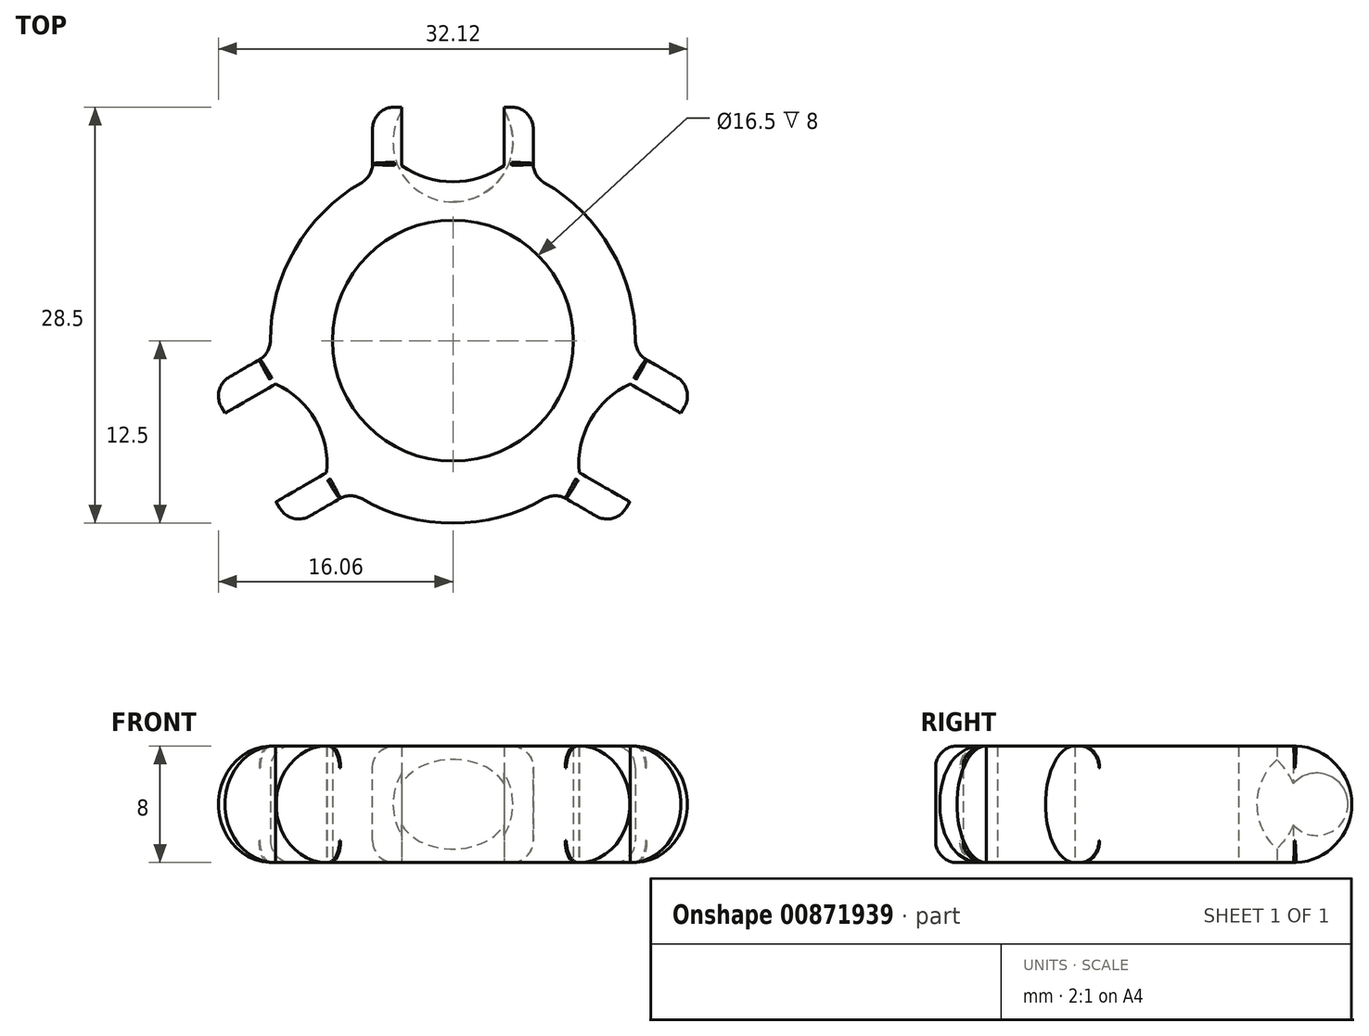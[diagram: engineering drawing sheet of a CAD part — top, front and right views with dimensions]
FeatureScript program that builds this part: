
annotation { "Feature Type Name" : "Feature", "Feature Type Description" : "" }
export const myFeature = defineFeature(function(context is Context, id is Id, definition is map)
    precondition{}
    {
        {
            var Q0;
            Q0=qCreatedBy(makeId("Top.planeOp"),FACE);
            var sketch = newSketch(context, id + "F0", { "sketchPlane" : qUnion([Q0])});
            skArc(sketch, "E0", {"start": v(-5.5, 11.22) * mm, "mid": v(-10.83, 6.25) * mm, "end": v(-12.47, -0.85) * mm});
            skLineSegment(sketch, "E1", {"start": v(0, 23.66) * mm, "end": v(0, -22.84) * mm, "construction": true});
            skLineSegment(sketch, "E2", {"start": v(-22.74, 0) * mm, "end": v(26.82, 0) * mm, "construction": true});
            skLineSegment(sketch, "E3", {"start": v(-3.5, 12) * mm, "end": v(-3.5, 16) * mm});
            skLineSegment(sketch, "E4", {"start": v(-3.5, 16) * mm, "end": v(-5.5, 16) * mm});
            skLineSegment(sketch, "E5", {"start": v(-5.5, 16) * mm, "end": v(-5.5, 11.22) * mm});
            skLineSegment(sketch, "E6.MirrorCS", {"start": v(3.5, 12) * mm, "end": v(3.5, 16) * mm});
            skLineSegment(sketch, "E7.MirrorCS", {"start": v(3.5, 16) * mm, "end": v(5.5, 16) * mm});
            skLineSegment(sketch, "E8.MirrorCS", {"start": v(5.5, 16) * mm, "end": v(5.5, 11.22) * mm});
            skLineSegment(sketch, "E9", {"start": v(-3.5, 12) * mm, "end": v(3.5, 12) * mm, "construction": true});
            skLineSegment(sketch, "E10", {"start": v(-3.5, 16) * mm, "end": v(3.5, 16) * mm, "construction": true});
            skPoint(sketch, "E11", {"position": v(0, 9.18) * mm});
            skLineSegment(sketch, "E12.1.0", {"start": v(-11.1, -12.76) * mm, "end": v(-6.97, -10.38) * mm});
            skLineSegment(sketch, "E12.1.1", {"start": v(-12.1, -11.03) * mm, "end": v(-11.1, -12.76) * mm});
            skLineSegment(sketch, "E12.1.2", {"start": v(-12.14, -2.97) * mm, "end": v(-15.6, -4.97) * mm});
            skLineSegment(sketch, "E12.1.3", {"start": v(-15.6, -4.97) * mm, "end": v(-16.6, -3.24) * mm});
            skLineSegment(sketch, "E12.1.4", {"start": v(-16.6, -3.24) * mm, "end": v(-12.47, -0.85) * mm});
            skLineSegment(sketch, "E12.1.5", {"start": v(-8.64, -9.03) * mm, "end": v(-12.1, -11.03) * mm});
            skLineSegment(sketch, "E12.2.0", {"start": v(16.6, -3.24) * mm, "end": v(12.47, -0.85) * mm});
            skLineSegment(sketch, "E12.2.1", {"start": v(15.6, -4.97) * mm, "end": v(16.6, -3.24) * mm});
            skLineSegment(sketch, "E12.2.2", {"start": v(8.64, -9.03) * mm, "end": v(12.1, -11.03) * mm});
            skLineSegment(sketch, "E12.2.3", {"start": v(12.1, -11.03) * mm, "end": v(11.1, -12.76) * mm});
            skLineSegment(sketch, "E12.2.4", {"start": v(11.1, -12.76) * mm, "end": v(6.97, -10.38) * mm});
            skLineSegment(sketch, "E12.2.5", {"start": v(12.14, -2.97) * mm, "end": v(15.6, -4.97) * mm});
            skArc(sketch, "E13.trimOffspring", {"start": v(12.47, -0.85) * mm, "mid": v(10.83, 6.25) * mm, "end": v(5.5, 11.22) * mm});
            skArc(sketch, "E14.trimOffspring", {"start": v(-6.97, -10.38) * mm, "mid": v(0, -12.5) * mm, "end": v(6.97, -10.38) * mm});
            skCircle(sketch, "E15", {"center": v(0, 0) * mm, "radius": 8.25 * mm});
            skArc(sketch, "E16", {"start": v(-3.5, 12) * mm, "mid": v(0, 10.87) * mm, "end": v(3.5, 12) * mm});
            skArc(sketch, "E17.1.0", {"start": v(-8.64, -9.03) * mm, "mid": v(-9.42, -5.44) * mm, "end": v(-12.14, -2.97) * mm});
            skArc(sketch, "E17.2.0", {"start": v(12.14, -2.97) * mm, "mid": v(9.42, -5.44) * mm, "end": v(8.64, -9.03) * mm});
            skSolve(sketch);
        }
        {
            var Q0;
            Q0=qCreatedBy(makeId("Front.planeOp"),FACE);
            var sketch = newSketch(context, id + "F1", { "sketchPlane" : qUnion([Q0])});
            skLineSegment(sketch, "E18", {"start": v(0, -15.32) * mm, "end": v(0, 34.97) * mm, "construction": true});
            skSolve(sketch);
        }
        {
            var Q0;
            Q0=qSketchRegion(id+"F0",true);
            extrude(context, id + "F2", {"entities" : qUnion([Q0]), "depth" : 8 * mm, "offsetDistance" : 25 * mm});
        }
        {
            var Q0;
            Q0=qCreatedBy(makeId("Top.planeOp"),FACE);
            cPlane(context, id + "F3", {"entities" : qUnion([Q0]), "cplaneType" : CPlaneType.OFFSET, "offset" : 4 * mm, "width" : 150 * mm, "height" : 150 * mm});
        }
        {
            var Q0;
            Q0=qCreatedBy(id+"F3.planeOp",FACE);
            var sketch = newSketch(context, id + "F4", { "sketchPlane" : qUnion([Q0])});
            skPoint(sketch, "E19.0", {"position": v(-3.5, 16) * mm});
            skPoint(sketch, "E20.0", {"position": v(3.5, 16) * mm});
            skLineSegment(sketch, "E21", {"start": v(0, 17.7) * mm, "end": v(0, 9.5) * mm});
            skArc(sketch, "E22", {"start": v(0, 17.7) * mm, "mid": v(-4.1, 13.6) * mm, "end": v(0, 9.5) * mm});
            skLineSegment(sketch, "E23", {"start": v(-3.5, 16) * mm, "end": v(3.5, 16) * mm, "construction": true});
            skLineSegment(sketch, "E24", {"start": v(0, 22.09) * mm, "end": v(0, 17.7) * mm, "construction": true});
            skPoint(sketch, "E25", {"position": v(0, 17.7) * mm});
            skSolve(sketch);
        }
        {
            var Q0;
            Q0=qSketchRegion(id+"F4",true);
            var Q1;
            Q1=sQuery(id+"F4.wireOp",EDGE,"E21");
            revolve(context, id + "F5", {"operationType" : NewBodyOperationType.REMOVE, "surfaceOperationType" : NewSurfaceOperationType.NEW, "entities" : qUnion([Q0]), "axis" : qUnion([Q1]), "revolveType" : RevolveType.FULL, "oppositeDirection" : true});
        }
        {
            var Q0;
            Q0=makeQuery(id+"F2.opExtrude","CAP_EDGE",EDGE,{"disambiguationData":[OSD([sQuery(id+"F0.wireOp",EDGE,"E4")])],"isStart":false});
            var Q1;
            Q1=makeQuery(id+"F2.opExtrude","CAP_EDGE",EDGE,{"disambiguationData":[OSD([sQuery(id+"F0.wireOp",EDGE,"E7.MirrorCS")])],"isStart":false});
            var Q2;
            Q2=makeQuery(id+"F2.opExtrude","CAP_EDGE",EDGE,{"disambiguationData":[OSD([sQuery(id+"F0.wireOp",EDGE,"E12.2.1")])],"isStart":false});
            var Q3;
            Q3=makeQuery(id+"F2.opExtrude","CAP_EDGE",EDGE,{"disambiguationData":[OSD([sQuery(id+"F0.wireOp",EDGE,"E12.2.3")])],"isStart":false});
            var Q4;
            Q4=makeQuery(id+"F2.opExtrude","CAP_EDGE",EDGE,{"disambiguationData":[OSD([sQuery(id+"F0.wireOp",EDGE,"E12.1.1")])],"isStart":false});
            var Q5;
            Q5=makeQuery(id+"F2.opExtrude","CAP_EDGE",EDGE,{"disambiguationData":[OSD([sQuery(id+"F0.wireOp",EDGE,"E12.1.3")])],"isStart":false});
            var Q6;
            Q6=makeQuery(id+"F2.opExtrude","CAP_EDGE",EDGE,{"disambiguationData":[OSD([sQuery(id+"F0.wireOp",EDGE,"E12.1.1")])],"isStart":true});
            var Q7;
            Q7=makeQuery(id+"F2.opExtrude","CAP_EDGE",EDGE,{"disambiguationData":[OSD([sQuery(id+"F0.wireOp",EDGE,"E12.1.3")])],"isStart":true});
            var Q8;
            Q8=makeQuery(id+"F2.opExtrude","CAP_EDGE",EDGE,{"disambiguationData":[OSD([sQuery(id+"F0.wireOp",EDGE,"E12.2.3")])],"isStart":true});
            var Q9;
            Q9=makeQuery(id+"F2.opExtrude","CAP_EDGE",EDGE,{"disambiguationData":[OSD([sQuery(id+"F0.wireOp",EDGE,"E12.2.1")])],"isStart":true});
            var Q10;
            Q10=makeQuery(id+"F2.opExtrude","CAP_EDGE",EDGE,{"disambiguationData":[OSD([sQuery(id+"F0.wireOp",EDGE,"E7.MirrorCS")])],"isStart":true});
            var Q11;
            Q11=makeQuery(id+"F2.opExtrude","CAP_EDGE",EDGE,{"disambiguationData":[OSD([sQuery(id+"F0.wireOp",EDGE,"E4")])],"isStart":true});
            fillet(context, id + "F6", {"entities" : qUnion([Q0, Q1, Q2, Q3, Q4, Q5, Q6, Q7, Q8, Q9, Q10, Q11]), "radius" : 4 * mm, "tangentPropagation" : true, "allowEdgeOverflow" : false});
        }
        {
            var Q0;
            Q0=makeQuery(id+"F2.opExtrude","SWEPT_EDGE",EDGE,{"disambiguationData":[OSD([sQuery(id+"F0.wireOp",EDGE,"E0"),sQuery(id+"F0.wireOp",EDGE,"E12.1.4")])]});
            var Q1;
            Q1=makeQuery(id+"F2.opExtrude","SWEPT_EDGE",EDGE,{"disambiguationData":[OSD([sQuery(id+"F0.wireOp",EDGE,"E0"),sQuery(id+"F0.wireOp",EDGE,"E5")])]});
            var Q2;
            Q2=makeQuery(id+"F2.opExtrude","SWEPT_EDGE",EDGE,{"disambiguationData":[OSD([sQuery(id+"F0.wireOp",EDGE,"E8.MirrorCS"),sQuery(id+"F0.wireOp",EDGE,"E13.trimOffspring")])]});
            var Q3;
            Q3=makeQuery(id+"F2.opExtrude","SWEPT_EDGE",EDGE,{"disambiguationData":[OSD([sQuery(id+"F0.wireOp",EDGE,"E12.2.0"),sQuery(id+"F0.wireOp",EDGE,"E13.trimOffspring")])]});
            var Q4;
            Q4=makeQuery(id+"F2.opExtrude","SWEPT_EDGE",EDGE,{"disambiguationData":[OSD([sQuery(id+"F0.wireOp",EDGE,"E12.2.4"),sQuery(id+"F0.wireOp",EDGE,"E14.trimOffspring")])]});
            var Q5;
            Q5=makeQuery(id+"F2.opExtrude","SWEPT_EDGE",EDGE,{"disambiguationData":[OSD([sQuery(id+"F0.wireOp",EDGE,"E12.1.0"),sQuery(id+"F0.wireOp",EDGE,"E14.trimOffspring")])]});
            fillet(context, id + "F7", {"entities" : qUnion([Q0, Q1, Q2, Q3, Q4, Q5]), "radius" : 1.5 * mm, "tangentPropagation" : true, "allowEdgeOverflow" : false});
        }
        {
            var Q0;
            Q0=makeQuery(id+"F2.opExtrude","CAP_EDGE",EDGE,{"disambiguationData":[OSD([sQuery(id+"F0.wireOp",EDGE,"E0")])],"isStart":true});
            var Q1;
            Q1=makeQuery(id+"F2.opExtrude","CAP_EDGE",EDGE,{"disambiguationData":[OSD([sQuery(id+"F0.wireOp",EDGE,"E14.trimOffspring")])],"isStart":true});
            var Q2;
            Q2=makeQuery(id+"F2.opExtrude","CAP_EDGE",EDGE,{"disambiguationData":[OSD([sQuery(id+"F0.wireOp",EDGE,"E13.trimOffspring")])],"isStart":true});
            fillet(context, id + "F8", {"entities" : qUnion([Q0, Q1, Q2]), "radius" : 1.5 * mm, "tangentPropagation" : true, "allowEdgeOverflow" : false});
        }
    });
